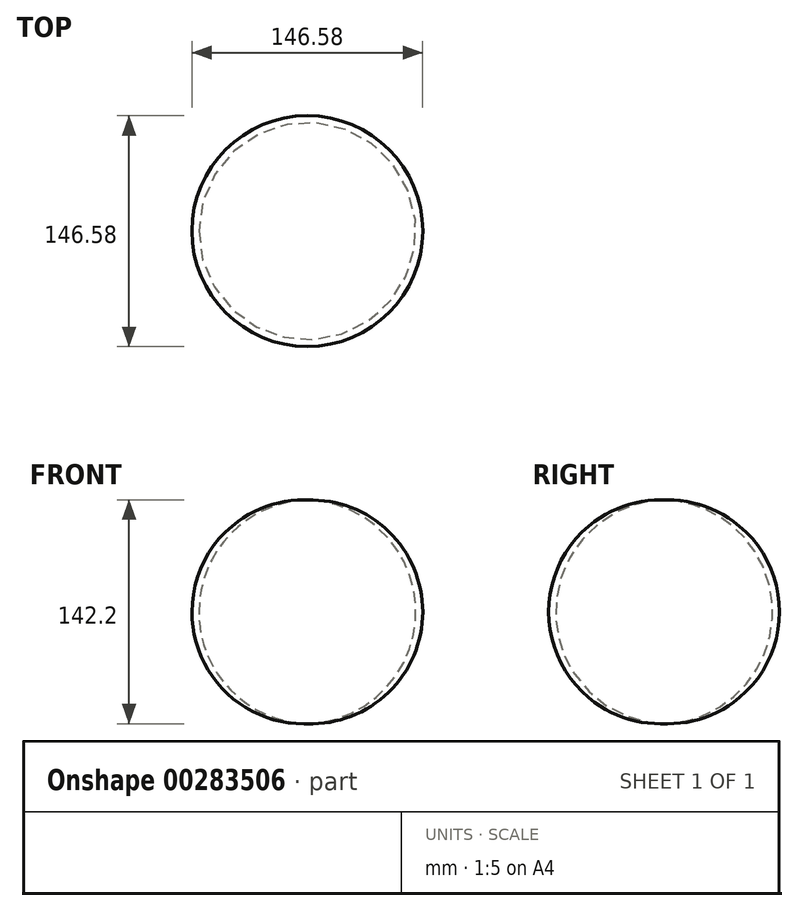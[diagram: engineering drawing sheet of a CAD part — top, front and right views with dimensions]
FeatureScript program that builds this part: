
annotation { "Feature Type Name" : "Feature", "Feature Type Description" : "" }
export const myFeature = defineFeature(function(context is Context, id is Id, definition is map)
    precondition{}
    {
        {
            var Q0;
            Q0=qCreatedBy(makeId("Front.planeOp"),FACE);
            var sketch = newSketch(context, id + "F0", { "sketchPlane" : qUnion([Q0])});
            skArc(sketch, "E0", {"start": v(2.2, -73.38) * mm, "mid": v(71.1, -2.31) * mm, "end": v(2.2, 68.75) * mm});
            skLineSegment(sketch, "E1", {"start": v(2.2, 68.75) * mm, "end": v(2.2, -76) * mm});
            skSolve(sketch);
        }
        {
            var Q0;
            {var subQ0=sQuery(id+"F0.wireOp",EDGE,"E0");Q0=makeQuery(id+"F0.imprint","IMPRINT",FACE,{"disambiguationData":[TD([[makeQuery(id+"F0.imprint","IMPRINT",EDGE,{"derivedFrom":subQ0}),1.0]])]});}
            var Q1;
            Q1=sQuery(id+"F0.wireOp",EDGE,"E1");
            revolve(context, id + "F1", {"entities" : qUnion([Q0]), "axis" : qUnion([Q1]), "revolveType" : RevolveType.FULL});
        }
    });
